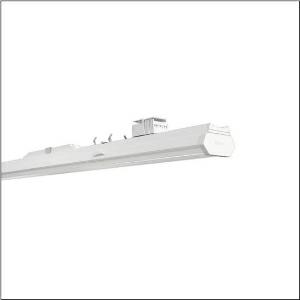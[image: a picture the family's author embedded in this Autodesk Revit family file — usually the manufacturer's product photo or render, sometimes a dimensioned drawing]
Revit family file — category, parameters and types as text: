
# Revit family: licross_r__11_protected_ho_51td12mn4f5m_c228
name_source: partatom
category: Lighting Fixtures
units: mm (PartAtom-declared; Revit-internal decimal feet)

## family parameters
Cut with Voids When Loaded = No
Host = Face
Light Source = No
Part Type = Normal
Room Calculation Point = No
Round Connector Dimension = Use Diameter
Shared = No

## types (1)
- --- (1 x LED, 15820 lm, 87.4 W, 4000K)
    Apparent Load = 87 VA
    CIE Flux Codes = 70 91 97 98 100
    Color Rendering = 80
    Color Temperature = 4000K
    Default Elevation = 1800 mm
    Description = Licross® 11 Protected HO, luminaire insert, of sheet steel, galvanised, coil coated, white, length: 1.500mm, width: 90mm, height: 101mm, LED rated luminous flux: 15.820lm, light colour: 840, control gear: ON/OFF Multilumen, control gear: ECG Multilumen, with plug, 3-pole, with phase selection, mains connection: 220..240V, AC, 50/60Hz, halogen-free wiring, primary light control with lens, of plastic, primary optical cover: cover, of PMMA, light emission: direct with ceiling illumination distribution, primary light characteristic: symmetric, protection rating (complete): IP54, insulation class (complete): insulation class I (protective earthing), certification: CE, ENEC, VDE, UKCA, protection symbol: D if used in an environment with non-conductive dust loads with corresponding accessories, impact resistance: IK06, permissible ambient temperature for indoor applications: -35..+35°C, corresponds to IFS (International Featured Standards) requirements for safety and quality in the food industry, reducing of maximum allowable ambient temperature of 5°C with ceiling mounting, LABS conformity tested according to VDMA 24364:2018-05, packaging unit: 1 piece
    Height = 92 mm
    Lamp = 1 x LED
    Lamp Light Flux = 15820 lm
    Lamp Power = 87.4 W
    Lamp count = 1
    Length = 1500 mm
    Luminous efficacy = 181 lm/W
    Manufacturer = Siteco
    ModVariant = No
    Model = 51TD12MN4F5M
    Mounting Place = Ceiling
    Mounting Type = Pendant
    Number of Poles = 1
    OnlyDefault = Yes
    Power Factor = 1
    Product Name = Licross® 11 Protected HO
    Product group = luminaire insert
    ProductGroupID = 902
    Protection Class = Protection class I
    Protection Degree = IP 54
    RLX_Detail_Level = 1
    RlxData = <blob elided: 22089 chars, md5=09a6a143>
    Socket = socket
    Standby Power = 0 W
    System Light Flux = 15820 lm
    System Power = 87 W
    Type Comments = factory setting: luminous flux: 100 % | (A | C | E) | 203 mA
    Type Image = l_1256145.jpg
    URL = http://relux.com
    VarID = @adj_003935
    Voltage = 0 V
    Weight = 0.00 kg
    Width = 88 mm

## geometry (parser evidence)
native form markers: Blend x4, Sweep x12
no freeform markers — native parametric forms only
